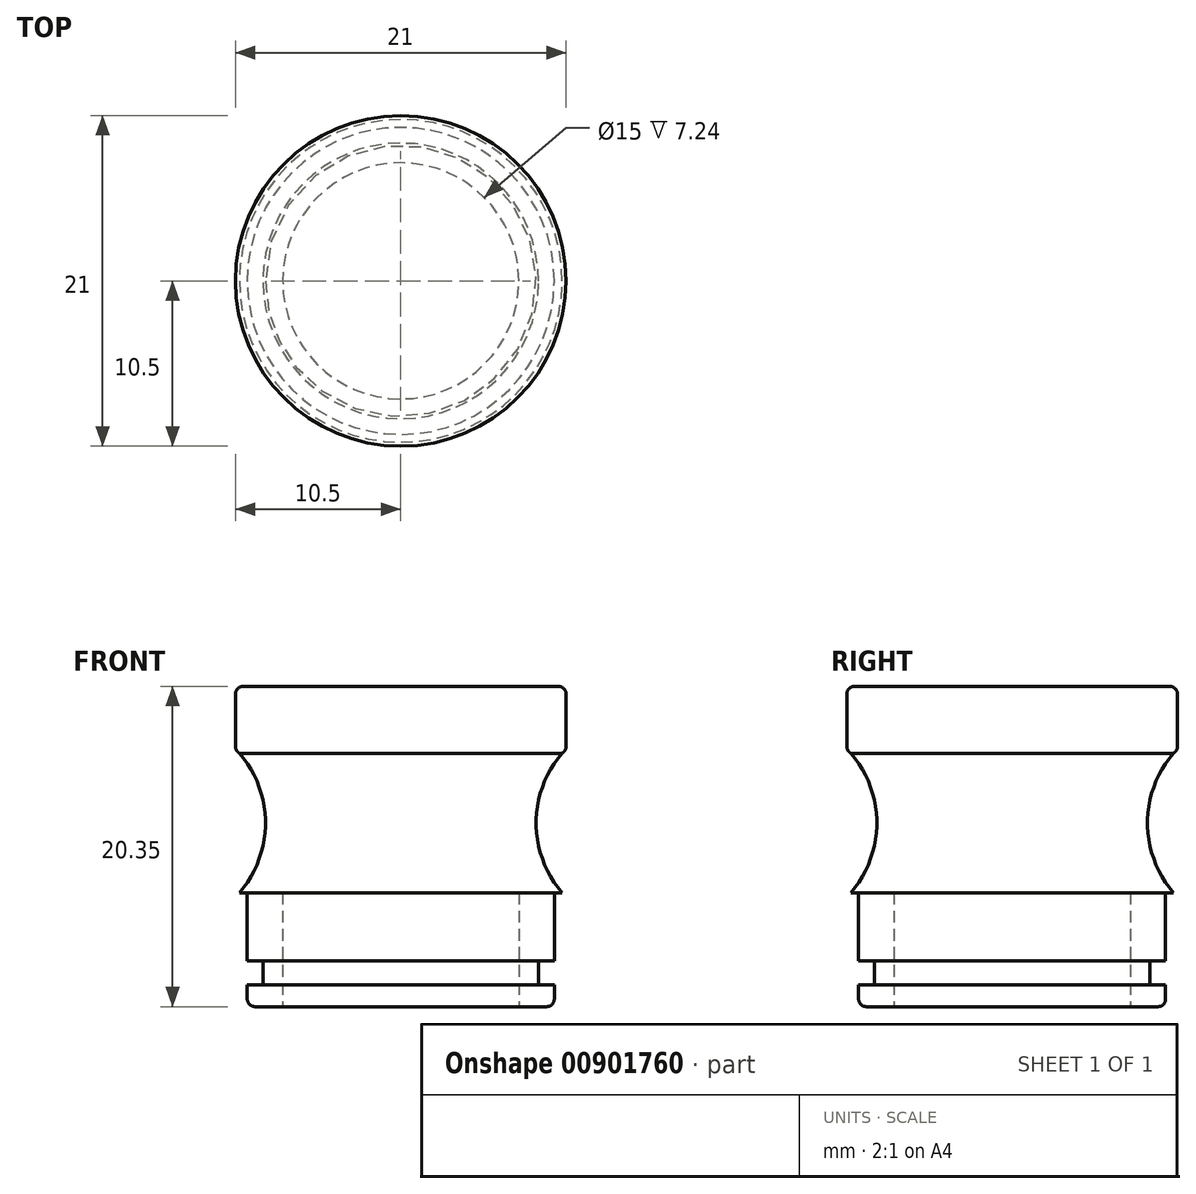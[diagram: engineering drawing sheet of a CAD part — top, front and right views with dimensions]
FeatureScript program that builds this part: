
annotation { "Feature Type Name" : "Feature", "Feature Type Description" : "" }
export const myFeature = defineFeature(function(context is Context, id is Id, definition is map)
    precondition{}
    {
        {
            var Q0;
            Q0=qCreatedBy(makeId("Right.planeOp"),FACE);
            var sketch = newSketch(context, id + "F0", { "sketchPlane" : qUnion([Q0])});
            skLineSegment(sketch, "E0.top", {"start": v(7.5, -7.24) * mm, "end": v(9.75, -7.24) * mm});
            skLineSegment(sketch, "E0.right", {"start": v(9.75, 0) * mm, "end": v(9.75, -4.34) * mm});
            skLineSegment(sketch, "E1.bottom", {"start": v(9.75, 0) * mm, "end": v(10.25, 0) * mm});
            skLineSegment(sketch, "E1.left", {"start": v(0, 0) * mm, "end": v(0, 8.86) * mm});
            skLineSegment(sketch, "E2.bottom", {"start": v(10.25, 8.86) * mm, "end": v(10.5, 8.86) * mm});
            skLineSegment(sketch, "E2.left", {"start": v(0, 8.86) * mm, "end": v(0, 13.1) * mm});
            skLineSegment(sketch, "E2.right", {"start": v(10.5, 8.86) * mm, "end": v(10.5, 13.1) * mm});
            skLineSegment(sketch, "E3.bottom", {"start": v(9.75, -4.34) * mm, "end": v(8.75, -4.34) * mm});
            skLineSegment(sketch, "E3.top", {"start": v(9.75, -5.84) * mm, "end": v(8.75, -5.84) * mm});
            skLineSegment(sketch, "E4.right", {"start": v(8.75, -4.34) * mm, "end": v(8.75, -5.84) * mm});
            skLineSegment(sketch, "E5.trimOffspring", {"start": v(9.75, -5.84) * mm, "end": v(9.75, -7.24) * mm});
            skArc(sketch, "E6", {"start": v(10.25, 8.86) * mm, "mid": v(8.6, 4.43) * mm, "end": v(10.25, 0) * mm});
            skLineSegment(sketch, "E7", {"start": v(10.5, 13.1) * mm, "end": v(0, 13.1) * mm});
            skLineSegment(sketch, "E8.bottom", {"start": v(0, 0) * mm, "end": v(7.5, 0) * mm});
            skLineSegment(sketch, "E8.right", {"start": v(7.5, 0) * mm, "end": v(7.5, -7.24) * mm});
            skSolve(sketch);
        }
        {
            var Q0;
            Q0=makeQuery(id+"F0.imprint","IMPRINT",FACE,{"disambiguationData":[TD([[makeQuery(id+"F0.imprint","IMPRINT",EDGE,{"derivedFrom":sQuery(id+"F0.wireOp",EDGE,"E0.top")}),1.0]])]});
            var Q1;
            Q1=sQuery(id+"F0.wireOp",EDGE,"E1.left");
            revolve(context, id + "F1", {"surfaceOperationType" : NewSurfaceOperationType.NEW, "entities" : qUnion([Q0]), "axis" : qUnion([Q1]), "revolveType" : RevolveType.FULL});
        }
        {
            var Q0;
            Q0=makeQuery(id+"F1.opRevolve","SWEPT_EDGE",EDGE,{"disambiguationData":[OSD([sQuery(id+"F0.wireOp",EDGE,"E2.right"),sQuery(id+"F0.wireOp",EDGE,"0sAw9EbU-71L9-2ekl-6xn4-OKHUJAQuSA2X")])]});
            var Q1;
            Q1=makeQuery(id+"F1.opRevolve","SWEPT_EDGE",EDGE,{"disambiguationData":[OSD([sQuery(id+"F0.wireOp",EDGE,"E2.bottom"),sQuery(id+"F0.wireOp",EDGE,"E2.right")])]});
            var Q2;
            Q2=makeQuery(id+"F1.opRevolve","SWEPT_EDGE",EDGE,{"disambiguationData":[OSD([sQuery(id+"F0.wireOp",EDGE,"E0.top"),sQuery(id+"F0.wireOp",EDGE,"E5.trimOffspring")])]});
            fillet(context, id + "F2", {"entities" : qUnion([Q0, Q1, Q2]), "radius" : 0.5 * mm, "tangentPropagation" : true, "allowEdgeOverflow" : false});
        }
    });
